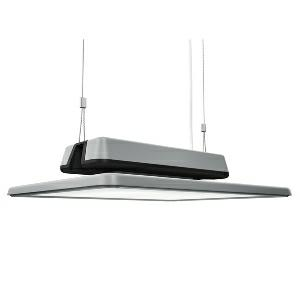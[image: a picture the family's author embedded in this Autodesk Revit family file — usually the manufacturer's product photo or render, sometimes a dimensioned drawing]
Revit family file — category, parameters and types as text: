
# Revit family: acaneo_-_hial_14000_850_w_dali_00737125_bb93
name_source: partatom
category: Lighting Fixtures
units: mm (PartAtom-declared; Revit-internal decimal feet)

## family parameters
Cut with Voids When Loaded = No
Host = Face
Light Source = No
Part Type = Normal
Room Calculation Point = No
Round Connector Dimension = Use Diameter
Shared = No

## types (1)
- ACANEO - HIAL 14000/850/W/DALI (1 x LED, 15000 lm, 5000K)
    Apparent Load = 90 VA
    Approval mark = CE
    CIE Flux Codes = 76 97 99 100 100
    Color Rendering = 80-89
    Color Temperature = 5000K
    Control Gear = Electronic ballast
    Default Elevation = 1800 mm
    Description = HIAL 14000/850/W/DALI|High bay luminaire|light source: LED|work equipment: Adjustable electronic ballast, digital DALI|connected load: 220-240 V, 50/60 Hz|Power consumption: approx. 90 W|power factor: approx. 0,987|luminous flux: 15000 lm|luminous efficacy: 166 lm/W|colour temperature: Cold white, ca. 5000 K|color rendering index (CRI): >= 80|chromaticity tolerance:  3 SDCM|System of protection: IP 65|class of protection: I|technology: Continuously dimmable|luminaire body|material: Aluminium|surface: Powder coatet|colour: White aluminium|lamp cover: Acrylic (PMMA), Clear|weight (net): approx. 8.2 kg|mains lead: Built-in plug RST 20i5 Einbau|Fastening: Available separately|Accessory: Junction box (RST 20i5)|minimum ambient temperature: -30 ░C|maximum ambient temperature: 70 ░C|glare control: Optics|unified glare rating(4H 8H): <=  22|
    Frequency = 50 Hz, 60 Hz
    Height = 125 mm
    Lamp = 1 x LED
    Lamp Light Flux = 15000 lm
    Lamp count = 1
    Length = 480 mm
    Luminous efficacy = 167 lm/W
    Manufacturer = Waldmann
    ModVariant = No
    Model = 00737125
    Mounting Place = Ceiling
    Mounting Type = Pendant
    Number of Poles = 1
    OnlyDefault = Yes
    Power Factor = 1
    Product Name = ACANEO - HIAL 14000/850/W/DALI
    Product group = High bay luminaire (industry)
    ProductGroupID = 901
    Protection Class = Protection class I
    Protection Degree = IP 65
    RLX_Detail_Level = 1
    RLX_Emergency_Light_Flux = 0 lm
    RLX_Emergency_Type = 0
    RLX_Emergency_Type_DB = No
    RlxData = <blob elided: 31229 chars, md5=6909cad2>
    Socket = socket
    Standby Power = 0 W
    System Light Flux = 15000 lm
    System Power = 90 W
    Type Comments = Product without accessories
    Type Image = acaneo-hial.jpg
    URL = http://relux.com
    VarID = ---
    Voltage = 230 V
    Voltage Range = 110-120 V, 220-240 V
    Weight = 0.00 kg
    Width = 405 mm

## geometry (parser evidence)
native form markers: Blend x4, Sweep x10
no freeform markers — native parametric forms only
